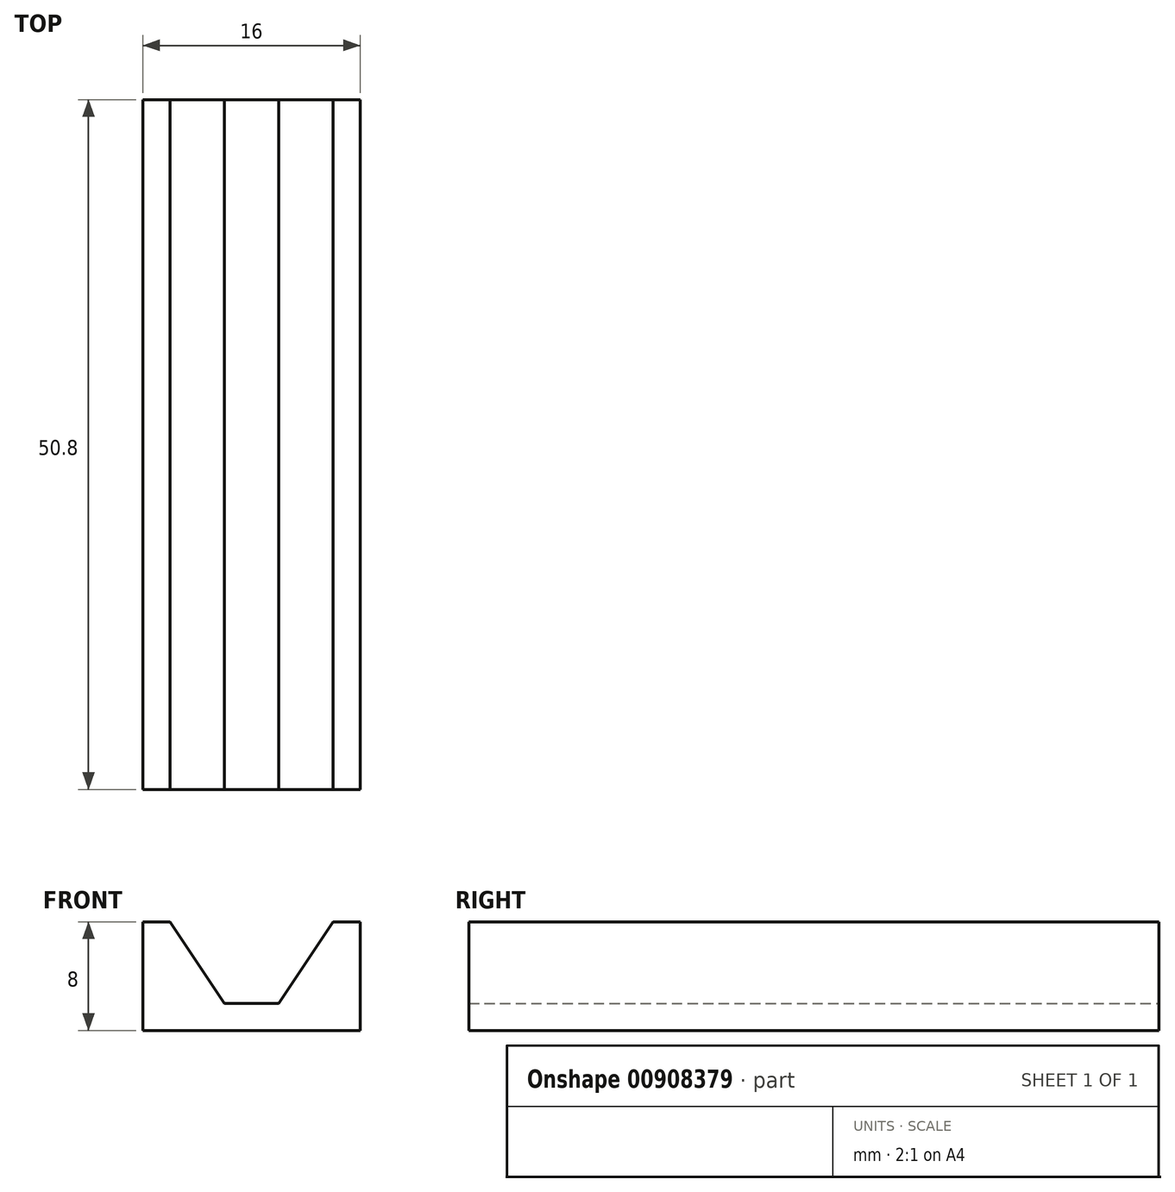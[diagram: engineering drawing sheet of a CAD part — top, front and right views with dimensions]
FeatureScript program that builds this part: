
annotation { "Feature Type Name" : "Feature", "Feature Type Description" : "" }
export const myFeature = defineFeature(function(context is Context, id is Id, definition is map)
    precondition{}
    {
        {
            var Q0;
            Q0=qCreatedBy(makeId("Front.planeOp"),FACE);
            var sketch = newSketch(context, id + "F0", { "sketchPlane" : qUnion([Q0])});
            skLineSegment(sketch, "E0.bottom", {"start": v(0, 0) * mm, "end": v(16, 0) * mm});
            skLineSegment(sketch, "E0.top", {"start": v(0, 8) * mm, "end": v(2, 8) * mm});
            skLineSegment(sketch, "E0.left", {"start": v(0, 0) * mm, "end": v(0, 8) * mm});
            skLineSegment(sketch, "E0.right", {"start": v(16, 0) * mm, "end": v(16, 8) * mm});
            skLineSegment(sketch, "E1", {"start": v(2, 8) * mm, "end": v(6, 2) * mm});
            skLineSegment(sketch, "E2", {"start": v(6, 2) * mm, "end": v(10, 2) * mm});
            skLineSegment(sketch, "E3", {"start": v(10, 2) * mm, "end": v(14, 8) * mm});
            skLineSegment(sketch, "E4.trimOffspring", {"start": v(14, 8) * mm, "end": v(16, 8) * mm});
            skSolve(sketch);
        }
        {
            var Q0;
            Q0=makeQuery(id+"F0.imprint","IMPRINT",FACE,{"disambiguationData":[TD([[makeQuery(id+"F0.imprint","IMPRINT",EDGE,{"derivedFrom":sQuery(id+"F0.wireOp",EDGE,"E0.bottom")}),1.0]])]});
            extrude(context, id + "F1", {"entities" : qUnion([Q0]), "depth" : 50.8 * mm, "offsetDistance" : 25.4 * mm});
        }
    });
